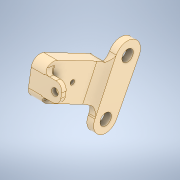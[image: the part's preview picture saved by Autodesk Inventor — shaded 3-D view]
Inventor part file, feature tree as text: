
AUTODESK INVENTOR PART (.ipt)
format: ipt  version: 2020 (Build 240168000, 168)  size: 282,112 bytes
history: native  units: in
note: dims shown in document units (in); Inventor stores cm internally (conversion verified against a paired STEP export)
features: sketch x8, extrude x5, fillet x5, projected_geometry x1
ambient origin geometry x8: Origin, YZ Plane, XZ Plane, XY Plane, X Axis, Y Axis, Z Axis, Center Point
bodies: Body1 (feature_tree)
feature tree (19):
  sketch  "Sketch3"  dims[d0=0.0039in d1=0.2362in d2=0.0in]
  sketch  "Sketch4"  dims[d3=0.315in d4=0.1575in d5=0.315in d6=0.0787in d7=0.0in d8=0.1181in]
  extrude  "Extrusion1"  Depth=0.2362in TaperAngle=0.0deg
  extrude  "Extrusion2"  Depth=0.1575in
  fillet  "Fillet1"  Radius=0.315in
  sketch  "Sketch7"  dims[d16=0.2008in d17=0.2008in]
  fillet  "Fillet2"  Radius=0.0787in
  fillet  "Fillet3"  Radius=0.1181in
  extrude  "Extrusion3"  Depth=0.1181in
  extrude  "Extrusion4"  Depth=0.0787in
  fillet  "Fillet4"  Radius=0.0787in
  fillet  "Fillet5"  Radius=0.0787in
  sketch  "Sketch9"  dims[d20=0.1969in]
  extrude  "Extrusion5"  Depth=0.2008in
  sketch  "Sketch5"  dims[d9=0.1102in d10=0.1181in]
  sketch  "Sketch6"  dims[d11=0.2047in d12=0.0787in d13=0.0787in d14=0.0787in d15=0.0in]
  sketch  "Sketch8"  dims[d18=0.1181in d19=0.0in]
  sketch  "Sketch10"  dims[d21=0.1969in d22=0.3717in d23=0.0787in d24=0.1181in d25=0.0in]
  projected_geometry  "Projected Loop2"
